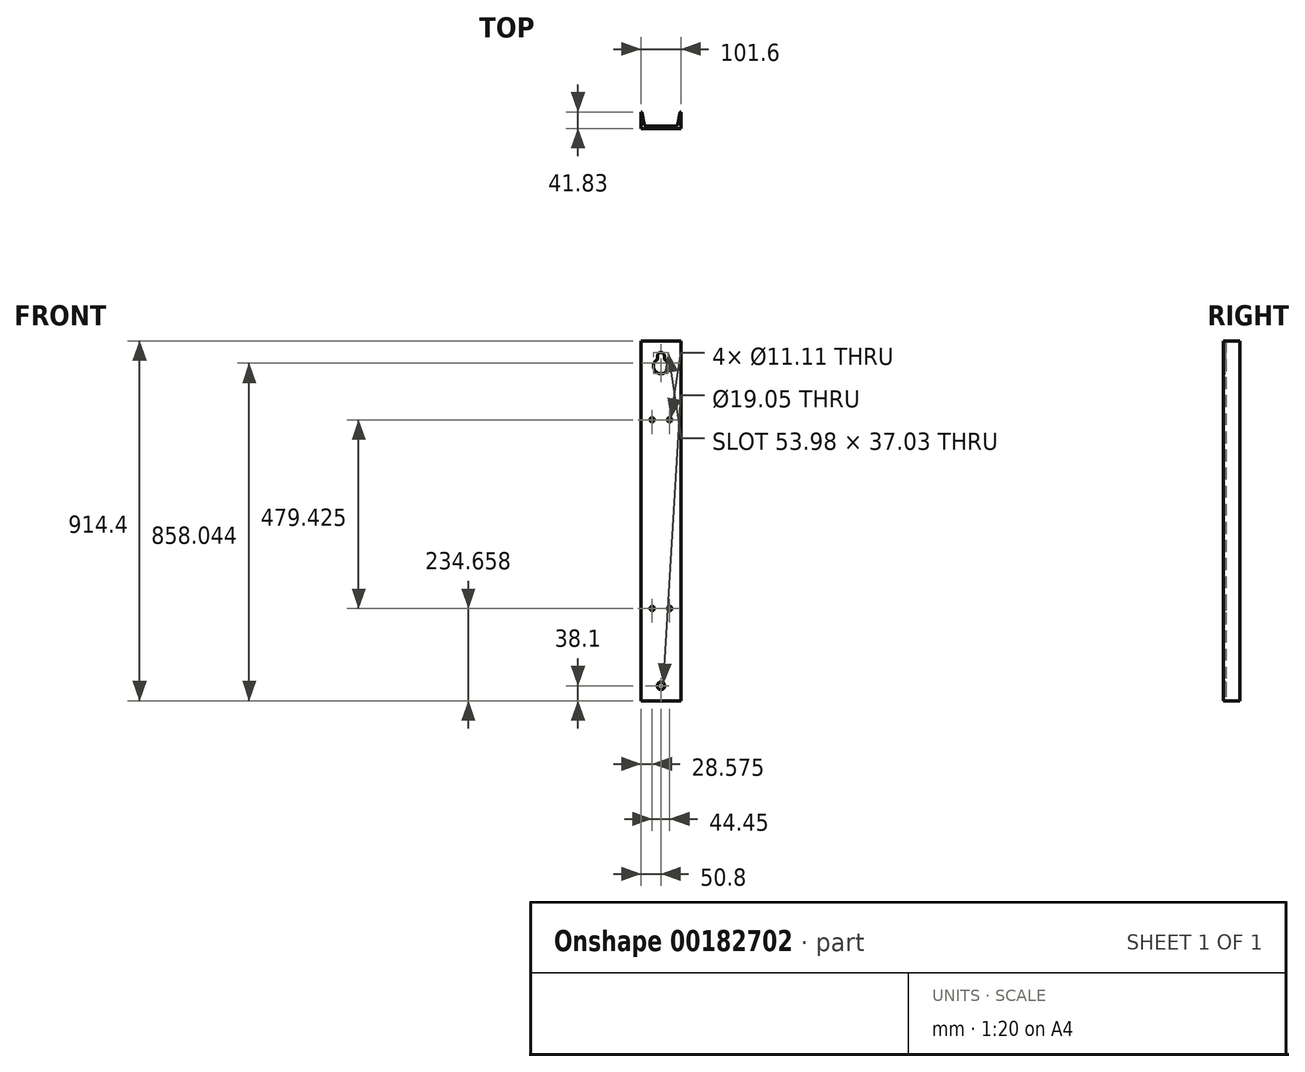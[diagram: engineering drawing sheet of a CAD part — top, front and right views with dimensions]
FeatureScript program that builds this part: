
annotation { "Feature Type Name" : "Feature", "Feature Type Description" : "" }
export const myFeature = defineFeature(function(context is Context, id is Id, definition is map)
    precondition{}
    {
        {
            var Q0;
            Q0=qCreatedBy(makeId("Top.planeOp"),FACE);
            var sketch = newSketch(context, id + "F0", { "sketchPlane" : qUnion([Q0])});
            skLineSegment(sketch, "E0", {"start": v(-50.8, 0) * mm, "end": v(50.8, 0) * mm});
            skLineSegment(sketch, "E1", {"start": v(50.8, 0) * mm, "end": v(50.8, 41.83) * mm});
            skLineSegment(sketch, "E2", {"start": v(-36.48, 6.27) * mm, "end": v(36.48, 6.27) * mm});
            skLineSegment(sketch, "E3", {"start": v(43.5, 12.22) * mm, "end": v(48.04, 39.5) * mm});
            skArc(sketch, "E4", {"start": v(50.8, 41.83) * mm, "mid": v(49, 41.17) * mm, "end": v(48.04, 39.5) * mm});
            skArc(sketch, "E5.filletArc", {"start": v(36.48, 6.27) * mm, "mid": v(41.08, 7.96) * mm, "end": v(43.5, 12.22) * mm});
            skArc(sketch, "E6.MirrorCS", {"start": v(-50.8, 41.83) * mm, "mid": v(-49, 41.17) * mm, "end": v(-48.04, 39.5) * mm});
            skLineSegment(sketch, "E7.MirrorCS", {"start": v(-43.5, 12.22) * mm, "end": v(-48.04, 39.5) * mm});
            skLineSegment(sketch, "E8.MirrorCS", {"start": v(-50.8, 0) * mm, "end": v(-50.8, 41.83) * mm});
            skArc(sketch, "E9.MirrorCS", {"start": v(-36.48, 6.27) * mm, "mid": v(-41.08, 7.96) * mm, "end": v(-43.5, 12.22) * mm});
            skSolve(sketch);
        }
        {
            var Q0;
            Q0=makeQuery(id+"F0.imprint","IMPRINT",FACE,{"disambiguationData":[TD([[makeQuery(id+"F0.imprint","IMPRINT",EDGE,{"derivedFrom":sQuery(id+"F0.wireOp",EDGE,"E0")}),1.0]])]});
            extrude(context, id + "F1", {"entities" : qUnion([Q0]), "depth" : 914.4 * mm});
        }
        {
            var Q0;
            Q0=makeQuery(id+"F1.opExtrude","SWEPT_FACE",FACE,{"disambiguationData":[OSD([sQuery(id+"F0.wireOp",EDGE,"E0")])]});
            var sketch = newSketch(context, id + "F2", { "sketchPlane" : qUnion([Q0])});
            skCircle(sketch, "E10", {"center": v(0, 38.1) * mm, "radius": 9.53 * mm});
            skSolve(sketch);
        }
        {
            var Q0;
            Q0=makeQuery(id+"F2.imprint","IMPRINT",FACE,{"disambiguationData":[TD([[makeQuery(id+"F2.imprint","IMPRINT",EDGE,{"derivedFrom":sQuery(id+"F2.wireOp",EDGE,"E10")}),1.0]])]});
            extrude(context, id + "F3", {"entities" : qUnion([Q0]), "operationType" : NewBodyOperationType.REMOVE, "endBound" : BoundingType.THROUGH_ALL, "oppositeDirection" : true, "depth" : 25.4 * mm});
        }
        {
            var Q0;
            Q0=makeQuery(id+"F1.opExtrude","SWEPT_FACE",FACE,{"disambiguationData":[OSD([sQuery(id+"F0.wireOp",EDGE,"E0")])]});
            var sketch = newSketch(context, id + "F4", { "sketchPlane" : qUnion([Q0])});
            skArc(sketch, "E11", {"start": v(8.73, 876.3) * mm, "mid": v(0, 885.03) * mm, "end": v(-8.73, 876.3) * mm});
            skLineSegment(sketch, "E12", {"start": v(-4.25, 868.68) * mm, "end": v(-4.25, 868.68) * mm});
            skLineSegment(sketch, "E13", {"start": v(-8.73, 876.3) * mm, "end": v(-8.73, 867.04) * mm});
            skLineSegment(sketch, "E14", {"start": v(8.73, 876.3) * mm, "end": v(8.73, 867.04) * mm});
            skArc(sketch, "E15.trimOffspring", {"start": v(-8.73, 867.04) * mm, "mid": v(0, 831.06) * mm, "end": v(8.73, 867.04) * mm});
            skSolve(sketch);
        }
        {
            var Q0;
            Q0=makeQuery(id+"F4.imprint","IMPRINT",FACE,{"disambiguationData":[TD([[makeQuery(id+"F4.imprint","IMPRINT",EDGE,{"derivedFrom":sQuery(id+"F4.wireOp",EDGE,"E11")}),1.0]])]});
            extrude(context, id + "F5", {"entities" : qUnion([Q0]), "operationType" : NewBodyOperationType.REMOVE, "endBound" : BoundingType.THROUGH_ALL, "oppositeDirection" : true, "depth" : 25.4 * mm});
        }
        {
            var Q0;
            Q0=makeQuery(id+"F1.opExtrude","SWEPT_FACE",FACE,{"disambiguationData":[OSD([sQuery(id+"F0.wireOp",EDGE,"E0")])]});
            var sketch = newSketch(context, id + "F6", { "sketchPlane" : qUnion([Q0])});
            skCircle(sketch, "E16", {"center": v(-22.23, 714.08) * mm, "radius": 5.56 * mm});
            skCircle(sketch, "E17", {"center": v(22.23, 714.08) * mm, "radius": 5.56 * mm});
            skCircle(sketch, "E18.MirrorC", {"center": v(-22.22, 234.66) * mm, "radius": 5.56 * mm});
            skCircle(sketch, "E19.MirrorC", {"center": v(22.23, 234.66) * mm, "radius": 5.56 * mm});
            skSolve(sketch);
        }
        {
            var Q0;
            Q0 = qSketchRegion(id + "F6", true);
            extrude(context, id + "F7", {"entities" : qUnion([Q0]), "operationType" : NewBodyOperationType.REMOVE, "endBound" : BoundingType.THROUGH_ALL, "oppositeDirection" : true, "depth" : 25.4 * mm});
        }
    });
